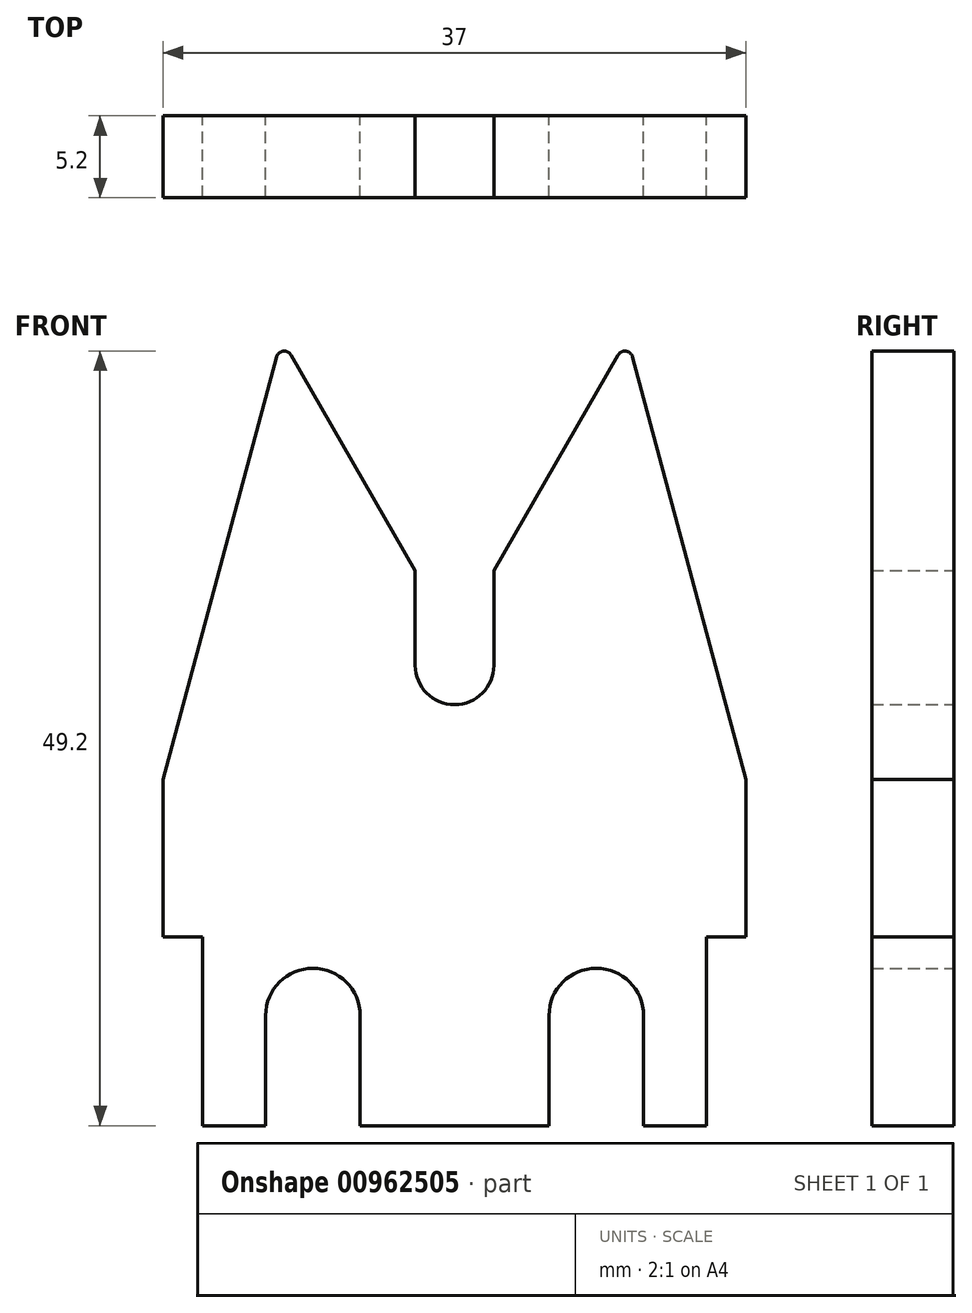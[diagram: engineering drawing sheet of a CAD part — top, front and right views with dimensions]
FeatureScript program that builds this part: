
annotation { "Feature Type Name" : "Feature", "Feature Type Description" : "" }
export const myFeature = defineFeature(function(context is Context, id is Id, definition is map)
    precondition{}
    {
        {
            var Q0;
            Q0=qCreatedBy(makeId("Front.planeOp"),FACE);
            var sketch = newSketch(context, id + "F0", { "sketchPlane" : qUnion([Q0])});
            skLineSegment(sketch, "E0", {"start": v(-35.08, 4.96) * mm, "end": v(-35.08, 16.96) * mm});
            skLineSegment(sketch, "E1", {"start": v(-35.08, 16.96) * mm, "end": v(-37.58, 16.96) * mm});
            skLineSegment(sketch, "E2", {"start": v(-37.58, 16.96) * mm, "end": v(-37.58, 26.96) * mm});
            skLineSegment(sketch, "E3", {"start": v(-35.08, 4.96) * mm, "end": v(-31.08, 4.96) * mm});
            skLineSegment(sketch, "E4", {"start": v(-37.58, 26.96) * mm, "end": v(-30.08, 54.96) * mm});
            skLineSegment(sketch, "E5", {"start": v(-30.08, 54.96) * mm, "end": v(-21.58, 40.24) * mm});
            skLineSegment(sketch, "E6", {"start": v(-21.58, 40.24) * mm, "end": v(-21.58, 34.2) * mm});
            skLineSegment(sketch, "E7", {"start": v(-19.08, 4.96) * mm, "end": v(-19.08, 34.2) * mm});
            skLineSegment(sketch, "E8.MirrorCS", {"start": v(-16.58, 40.24) * mm, "end": v(-16.58, 34.2) * mm});
            skLineSegment(sketch, "E9.MirrorCS", {"start": v(-8.08, 54.96) * mm, "end": v(-16.58, 40.24) * mm});
            skLineSegment(sketch, "E10.MirrorCS", {"start": v(-0.58, 26.96) * mm, "end": v(-8.08, 54.96) * mm});
            skLineSegment(sketch, "E11.MirrorCS", {"start": v(-0.58, 16.96) * mm, "end": v(-0.58, 26.96) * mm});
            skLineSegment(sketch, "E12.MirrorCS", {"start": v(-3.08, 4.96) * mm, "end": v(-3.08, 16.96) * mm});
            skLineSegment(sketch, "E13.MirrorCS", {"start": v(-3.08, 4.96) * mm, "end": v(-7.08, 4.96) * mm});
            skLineSegment(sketch, "E14.MirrorCS", {"start": v(-3.08, 16.96) * mm, "end": v(-0.58, 16.96) * mm});
            skArc(sketch, "E15", {"start": v(-21.58, 34.2) * mm, "mid": v(-19.08, 31.7) * mm, "end": v(-16.58, 34.2) * mm});
            skPoint(sketch, "E16.MirrorCS.start.orphan", {"position": v(-16.58, 34.2) * mm});
            skLineSegment(sketch, "E17", {"start": v(-31.08, 4.96) * mm, "end": v(-31.08, 11.96) * mm});
            skLineSegment(sketch, "E18", {"start": v(-25.08, 11.96) * mm, "end": v(-25.08, 4.96) * mm});
            skArc(sketch, "E19", {"start": v(-25.08, 11.96) * mm, "mid": v(-28.08, 14.96) * mm, "end": v(-31.08, 11.96) * mm});
            skLineSegment(sketch, "E20.trimOffspring", {"start": v(-25.08, 4.96) * mm, "end": v(-19.08, 4.96) * mm});
            skLineSegment(sketch, "E21.MirrorCS", {"start": v(-13.08, 11.96) * mm, "end": v(-13.08, 4.96) * mm});
            skArc(sketch, "E22.MirrorCS", {"start": v(-13.08, 11.96) * mm, "mid": v(-10.08, 14.96) * mm, "end": v(-7.08, 11.96) * mm});
            skLineSegment(sketch, "E23.MirrorCS", {"start": v(-7.08, 4.96) * mm, "end": v(-7.08, 11.96) * mm});
            skLineSegment(sketch, "E24.trimOffspring", {"start": v(-13.08, 4.96) * mm, "end": v(-19.08, 4.96) * mm});
            skSolve(sketch);
        }
        {
            var Q0;
            Q0=makeQuery(id+"F0.imprint","IMPRINT",FACE,{"disambiguationData":[TD([[makeQuery(id+"F0.imprint","IMPRINT",EDGE,{"derivedFrom":sQuery(id+"F0.wireOp",EDGE,"E0")}),-1.0]])]});
            var Q1;
            {var subQ1=sQuery(id+"F0.wireOp",EDGE,"E8.MirrorCS");Q1=makeQuery(id+"F0.imprint","IMPRINT",FACE,{"disambiguationData":[TD([[makeQuery(id+"F0.imprint","IMPRINT",EDGE,{"derivedFrom":subQ1}),1.0]])]});}
            extrude(context, id + "F1", {"entities" : qUnion([Q0, Q1]), "depth" : 5.2 * mm, "offsetDistance" : 25 * mm});
        }
        {
            var Q0;
            Q0=makeQuery(id+"F1.opExtrude","SWEPT_EDGE",EDGE,{"disambiguationData":[OSD([sQuery(id+"F0.wireOp",EDGE,"E4"),sQuery(id+"F0.wireOp",EDGE,"E5")])]});
            var Q1;
            Q1=makeQuery(id+"F1.opExtrude","SWEPT_EDGE",EDGE,{"disambiguationData":[OSD([sQuery(id+"F0.wireOp",EDGE,"E9.MirrorCS"),sQuery(id+"F0.wireOp",EDGE,"E10.MirrorCS")])]});
            fillet(context, id + "F2", {"entities" : qUnion([Q0, Q1]), "radius" : 0.5 * mm, "tangentPropagation" : true, "allowEdgeOverflow" : false});
        }
    });
